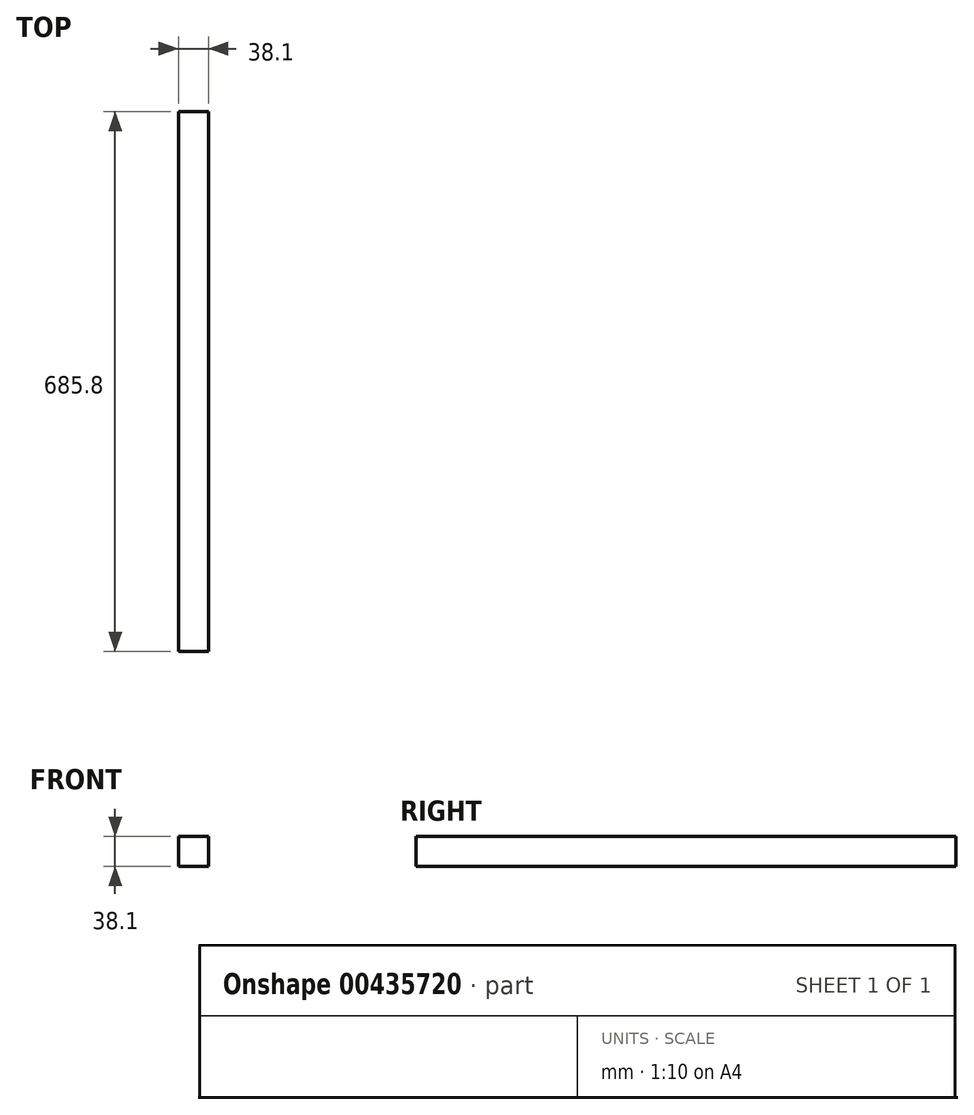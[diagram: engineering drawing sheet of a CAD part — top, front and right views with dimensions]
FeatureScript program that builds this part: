
annotation { "Feature Type Name" : "Feature", "Feature Type Description" : "" }
export const myFeature = defineFeature(function(context is Context, id is Id, definition is map)
    precondition{}
    {
        {
            var Q0;
            Q0=qCreatedBy(makeId("Front.planeOp"),FACE);
            var sketch = newSketch(context, id + "F0", { "sketchPlane" : qUnion([Q0])});
            skLineSegment(sketch, "E0.bottom", {"start": v(19.05, -19.05) * mm, "end": v(-19.05, -19.05) * mm});
            skLineSegment(sketch, "E0.top", {"start": v(19.05, 19.05) * mm, "end": v(-19.05, 19.05) * mm});
            skLineSegment(sketch, "E0.left", {"start": v(19.05, -19.05) * mm, "end": v(19.05, 19.05) * mm});
            skLineSegment(sketch, "E0.right", {"start": v(-19.05, -19.05) * mm, "end": v(-19.05, 19.05) * mm});
            skPoint(sketch, "E0.middle", {"position": v(0, 0) * mm});
            skSolve(sketch);
        }
        {
            var Q0;
            Q0=makeQuery(id+"F0.imprint","IMPRINT",FACE,{"disambiguationData":[TD([[makeQuery(id+"F0.imprint","IMPRINT",EDGE,{"derivedFrom":sQuery(id+"F0.wireOp",EDGE,"E0.bottom")}),-1.0]])]});
            extrude(context, id + "F1", {"entities" : qUnion([Q0]), "endBound" : BoundingType.SYMMETRIC, "depth" : 685.8 * mm});
        }
    });
